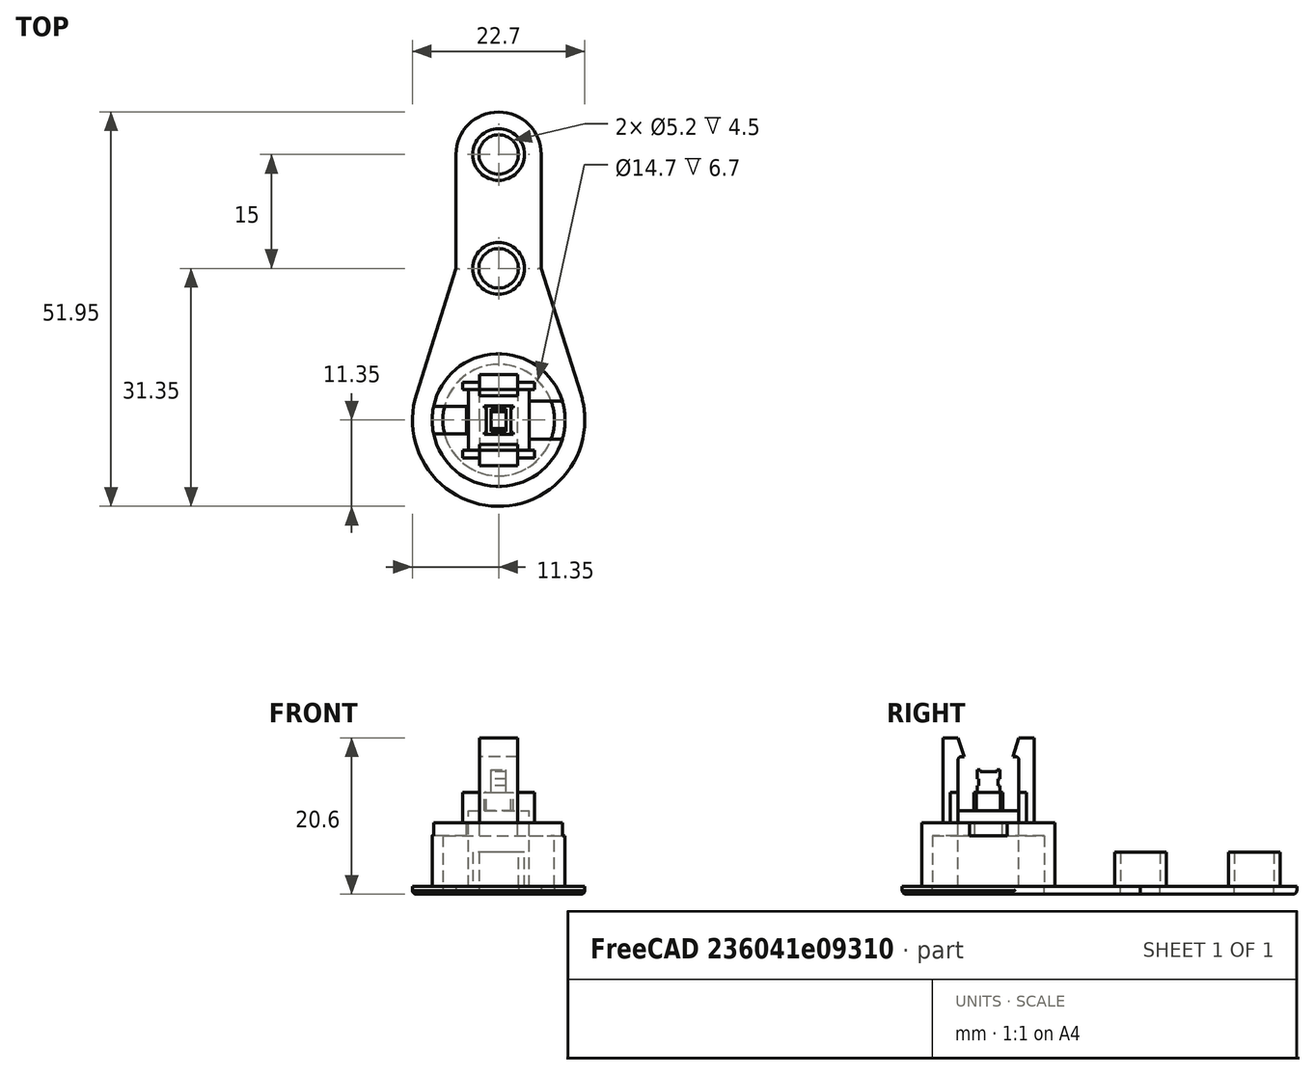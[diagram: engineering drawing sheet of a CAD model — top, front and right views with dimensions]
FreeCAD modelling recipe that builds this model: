
FCSTD DOCUMENT  (FreeCAD 0.18R13728 (Git))
Label: test113_powerbutton
License: All rights reserved
LicenseURL: http://en.wikipedia.org/wiki/All_rights_reserved
objects: Sketcher::SketchObject×12, PartDesign::Pad×10, PartDesign::Body×3, PartDesign::Fillet×2, Part::MultiFuse×2, PartDesign::Pocket×1, PartDesign::Plane×1, Mesh::Feature×1, Part::Extrusion×1, Part::Fillet×1, PartDesign::FeatureBase×1
note: 45 computed .brp shape members not serialized (recipe doc carries the construction recipe); baked Part::Feature solids carry a one-line shape summary decoded from their .brp

FEATURE [Sketcher::SketchObject] Sketch
  MapMode = 5
  Support = -> [XY_Plane]
  sketch-geometry (4):
    g0: LineSegment StartX=-4 StartY=-4 StartZ=0 EndX=4 EndY=-4 EndZ=0
    g1: LineSegment StartX=4 StartY=-4 StartZ=0 EndX=4 EndY=4 EndZ=0
    g2: LineSegment StartX=4 StartY=4 StartZ=0 EndX=-4 EndY=4 EndZ=0
    g3: LineSegment StartX=-4 StartY=4 StartZ=0 EndX=-4 EndY=-4 EndZ=0
  constraints (11):
    c: Coincident(g0,g1)
    c: Coincident(g1,g2)
    c: Coincident(g2,g3)
    c: Coincident(g3,g0)
    c: Horizontal(g0)
    c: Horizontal(g2)
    c: Vertical(g1)
    c: Vertical(g3)
    c: Equal(g2,g3)
    c: Symmetric(g2,g0,g-1)
    c: Distance(g2) = 8
FEATURE [PartDesign::Pad] Pad
  Length = 10
  Length2 = 100
  Profile = -> Sketch
  Type = 0
FEATURE [Sketcher::SketchObject] Sketch001
  MapMode = 5
  Placement = pos=(0,0,10) rot=(0,0,1;0rad)
  Support = -> [Pad]
  sketch-geometry (12):
    g0: LineSegment StartX=-1.9 StartY=1.9 StartZ=0 EndX=1.9 EndY=1.9 EndZ=0
    g1: LineSegment StartX=1.9 StartY=-1.9 StartZ=0 EndX=-1.9 EndY=-1.9 EndZ=0
    g2: LineSegment StartX=1.9 StartY=1.6 StartZ=0 EndX=1.6 EndY=1.6 EndZ=0
    g3: LineSegment StartX=1.6 StartY=1.6 StartZ=0 EndX=1.6 EndY=-1.6 EndZ=0
    g4: LineSegment StartX=1.6 StartY=-1.6 StartZ=0 EndX=1.9 EndY=-1.6 EndZ=0
    g5: LineSegment StartX=-1.9 StartY=-1.6 StartZ=0 EndX=-1.6 EndY=-1.6 EndZ=0
    g6: LineSegment StartX=-1.6 StartY=-1.6 StartZ=0 EndX=-1.6 EndY=1.6 EndZ=0
    g7: LineSegment StartX=-1.6 StartY=1.6 StartZ=0 EndX=-1.9 EndY=1.6 EndZ=0
    g8: LineSegment StartX=-1.9 StartY=1.6 StartZ=0 EndX=-1.9 EndY=1.9 EndZ=0
    g9: LineSegment StartX=1.9 StartY=1.6 StartZ=0 EndX=1.9 EndY=1.9 EndZ=0
    g10: LineSegment StartX=1.9 StartY=-1.6 StartZ=0 EndX=1.9 EndY=-1.9 EndZ=0
    g11: LineSegment StartX=-1.9 StartY=-1.9 StartZ=0 EndX=-1.9 EndY=-1.6 EndZ=0
  constraints (36):
    c: Horizontal(g0)
    c: Horizontal(g1)
    c: Distance(g0) = 3.8
    c: Coincident(g2,g3)
    c: Coincident(g3,g4)
    c: Horizontal(g2)
    c: Horizontal(g4)
    c: Vertical(g3)
    c: Coincident(g5,g6)
    c: Coincident(g6,g7)
    c: Horizontal(g5)
    c: Horizontal(g7)
    c: Vertical(g6)
    c: Coincident(g8,g7)
    c: Coincident(g8,g0)
    c: Vertical(g8)
    c: Coincident(g9,g2)
    c: Coincident(g9,g0)
    c: Vertical(g9)
    c: Coincident(g10,g4)
    c: Coincident(g10,g1)
    c: Coincident(g11,g1)
    c: Coincident(g11,g5)
    c: Vertical(g11)
    c: Vertical(g10)
    c: Symmetric(g0,g1,g-1)
    c: Equal(g5,g7)
    c: Equal(g5,g2)
    c: Equal(g5,g4)
    c: Equal(g6,g3)
    c: Equal(g11,g10)
    c: Equal(g11,g8)
    c: Equal(g11,g9)
    c: Distance(g8) = 0.3
    c: Distance(g7) = 0.3
    c: Distance(g1,g0) = 3.8
FEATURE [PartDesign::Pad] Pad001
  BaseFeature = -> Pad
  Length = 2.4
  Length2 = 100
  Profile = -> Sketch001
  Type = 0
FEATURE [Sketcher::SketchObject] Sketch002
  MapMode = 5
  Placement = pos=(0,0,12.4) rot=(0,0,1;0rad)
  Support = -> [Pad001]
  sketch-geometry (4):
    g0: LineSegment StartX=-1 StartY=-1.5 StartZ=0 EndX=1 EndY=-1.5 EndZ=0
    g1: LineSegment StartX=1 StartY=-1.5 StartZ=0 EndX=1 EndY=1.5 EndZ=0
    g2: LineSegment StartX=1 StartY=1.5 StartZ=0 EndX=-1 EndY=1.5 EndZ=0
    g3: LineSegment StartX=-1 StartY=1.5 StartZ=0 EndX=-1 EndY=-1.5 EndZ=0
  constraints (11):
    c: Coincident(g0,g1)
    c: Coincident(g1,g2)
    c: Coincident(g2,g3)
    c: Coincident(g3,g0)
    c: Horizontal(g0)
    c: Horizontal(g2)
    c: Vertical(g1)
    c: Vertical(g3)
    c: Symmetric(g0,g1,g-1)
    c: Distance(g2) = 2
    c: Distance(g1) = 3
FEATURE [PartDesign::Pad] Pad002
  BaseFeature = -> Pad001
  Length = 3
  Length2 = 100
  Profile = -> Sketch002
  Type = 0
FEATURE [Sketcher::SketchObject] Sketch003
  ExternalGeometry = -> [Pad002]
  MapMode = 5
  Placement = pos=(1,0,0) rot=(0.57735,0.57735,0.57735;2.0944rad)
  Support = -> [Pad002]
  sketch-geometry (12):
    g0: LineSegment StartX=-1.5 StartY=13.3 StartZ=0 EndX=-1.25 EndY=13.3 EndZ=0
    g1: LineSegment StartX=-1.25 StartY=13.3 StartZ=0 EndX=-1.25 EndY=14.2 EndZ=0
    g2: LineSegment StartX=-1.25 StartY=14.2 StartZ=0 EndX=-1.5 EndY=14.2 EndZ=0
    g3: LineSegment StartX=-1.5 StartY=14.2 StartZ=0 EndX=-1.5 EndY=13.3 EndZ=0
    g4: LineSegment StartX=1.5 StartY=13.3 StartZ=0 EndX=1.25 EndY=13.3 EndZ=0
    g5: LineSegment StartX=1.25 StartY=13.3 StartZ=0 EndX=1.25 EndY=14.2 EndZ=0
    g6: LineSegment StartX=1.25 StartY=14.2 StartZ=0 EndX=1.5 EndY=14.2 EndZ=0
    g7: LineSegment StartX=1.5 StartY=14.2 StartZ=0 EndX=1.5 EndY=13.3 EndZ=0
    g8: LineSegment StartX=-1.1 StartY=15.4 StartZ=0 EndX=1.1 EndY=15.4 EndZ=0
    g9: LineSegment StartX=1.1 StartY=15.4 StartZ=0 EndX=1.1 EndY=15.1 EndZ=0
    g10: LineSegment StartX=1.1 StartY=15.1 StartZ=0 EndX=-1.1 EndY=15.1 EndZ=0
    g11: LineSegment StartX=-1.1 StartY=15.1 StartZ=0 EndX=-1.1 EndY=15.4 EndZ=0
  constraints (36):
    c: Coincident(g0,g1)
    c: Coincident(g1,g2)
    c: Coincident(g2,g3)
    c: Coincident(g3,g0)
    c: Horizontal(g0)
    c: Horizontal(g2)
    c: Vertical(g1)
    c: Vertical(g3)
    c: PointOnObject(g0,g-3)
    c: Coincident(g4,g5)
    c: Coincident(g5,g6)
    c: Coincident(g6,g7)
    c: Coincident(g7,g4)
    c: Horizontal(g4)
    c: Horizontal(g6)
    c: Vertical(g5)
    c: Vertical(g7)
    c: PointOnObject(g4,g-5)
    c: Coincident(g8,g9)
    c: Coincident(g9,g10)
    c: Coincident(g10,g11)
    c: Coincident(g11,g8)
    c: Horizontal(g8)
    c: Horizontal(g10)
    c: Vertical(g9)
    c: Vertical(g11)
    c: PointOnObject(g8,g-6)
    c: Distance(g0,g4) = 2.5
    c: Equal(g2,g6)
    c: Equal(g5,g1)
    c: DistanceY(g0,g4) = 0
    c: DistanceY(g-4,g0) = 0.9
    c: Distance(g10) = 2.2
    c: Distance(g11) = 0.3
    c: Symmetric(g10,g9,g-2)
    c: Distance(g1) = 0.9
FEATURE [PartDesign::Pocket] Pocket
  BaseFeature = -> Pad002
  Length = 5
  Length2 = 100
  Profile = -> Sketch003
  Type = 1
FEATURE [PartDesign::Body] Body  label="Switch"
  Group = -> [Sketch,Pad,Sketch001,Pad001,Sketch002,Pad002,Sketch003,Pocket]
  Origin = -> Origin
  Tip = -> Pocket
FEATURE [Sketcher::SketchObject] Sketch004
  MapMode = 5
  Support = -> [XY_Plane002]
  sketch-geometry (2):
    g0: Circle CenterX=0 CenterY=0 CenterZ=0 NormalX=0 NormalY=0 NormalZ=1 AngleXU=0 Radius=7.35
    g1: Circle CenterX=0 CenterY=0 CenterZ=0 NormalX=0 NormalY=0 NormalZ=1 AngleXU=0 Radius=8.75
  constraints (4):
    c: Coincident(g0,g-1)
    c: Radius(g0) = 7.35
    c: Coincident(g1,g-1)
    c: Radius(g1) = 8.75
FEATURE [PartDesign::Pad] Pad003
  Length = 6.7
  Length2 = 100
  Profile = -> Sketch004
  Type = 0
FEATURE [Sketcher::SketchObject] Sketch005
  ExternalGeometry = -> [Pad003]
  MapMode = 5
  Placement = pos=(0,0,6.7) rot=(0,0,1;0rad)
  Support = -> [Pad003]
  sketch-geometry (20):
    g0: ArcOfCircle CenterX=0 CenterY=0 CenterZ=0 NormalX=0 NormalY=0 NormalZ=1 AngleXU=0 Radius=8.75 StartAngle=0.289752 EndAngle=2.9344
    g1: LineSegment StartX=-4.2276 StartY=0 StartZ=0 EndX=-4.2276 EndY=1.8 EndZ=0
    g2: LineSegment StartX=-4.2276 StartY=1.8 StartZ=0 EndX=-8.56286 EndY=1.8 EndZ=0
    g3: LineSegment StartX=4.05 StartY=0 StartZ=0 EndX=4.05 EndY=2.5 EndZ=0
    g4: LineSegment StartX=4.05 StartY=2.5 StartZ=0 EndX=8.38525 EndY=2.5 EndZ=0
    g5: GeomPoint X=8.75 Y=0 Z=0
    g6: GeomPoint X=-8.75 Y=0 Z=0
    g7: LineSegment StartX=-2.5 StartY=0 StartZ=0 EndX=-2.5 EndY=4 EndZ=0
    g8: LineSegment StartX=-2.5 StartY=4 StartZ=0 EndX=2.5 EndY=4 EndZ=0
    g9: LineSegment StartX=2.5 StartY=4 StartZ=0 EndX=2.5 EndY=0 EndZ=0
    g10: ArcOfCircle CenterX=0 CenterY=0 CenterZ=0 NormalX=0 NormalY=0 NormalZ=1 AngleXU=0 Radius=8.75 StartAngle=3.34879 EndAngle=5.99343
    g11: LineSegment StartX=-4.2276 StartY=0 StartZ=0 EndX=-4.2276 EndY=-1.8 EndZ=0
    g12: LineSegment StartX=-4.2276 StartY=-1.8 StartZ=0 EndX=-8.56286 EndY=-1.8 EndZ=0
    g13: LineSegment StartX=4.05 StartY=0 StartZ=0 EndX=4.05 EndY=-2.5 EndZ=0
    g14: LineSegment StartX=4.05 StartY=-2.5 StartZ=0 EndX=8.38525 EndY=-2.5 EndZ=0
    g15: GeomPoint X=8.75 Y=0 Z=0
    g16: GeomPoint X=-8.75 Y=0 Z=0
    g17: LineSegment StartX=-2.5 StartY=0 StartZ=0 EndX=-2.5 EndY=-4 EndZ=0
    g18: LineSegment StartX=-2.5 StartY=-4 StartZ=0 EndX=2.5 EndY=-4 EndZ=0
    g19: LineSegment StartX=2.5 StartY=-4 StartZ=0 EndX=2.5 EndY=0 EndZ=0
  constraints (55):
    c: Coincident(g0,g-1)
    c: PointOnObject(g0,g-3)
    c: PointOnObject(g1,g-1)
    c: Vertical(g1)
    c: Coincident(g1,g2)
    c: Coincident(g2,g0)
    c: Horizontal(g2)
    c: PointOnObject(g3,g-1)
    c: Vertical(g3)
    c: Coincident(g3,g4)
    c: Coincident(g4,g0)
    c: Horizontal(g4)
    c: PointOnObject(g5,g-3)
    c: PointOnObject(g6,g-3)
    c: PointOnObject(g6,g-1)
    c: PointOnObject(g5,g-1)
    c: DistanceX(g3,g5) = 4.7
    c: Distance(g3) = 2.5
    c: Distance(g1) = 1.8
    c: PointOnObject(g7,g-1)
    c: Vertical(g7)
    c: Coincident(g7,g8)
    c: Horizontal(g8)
    c: Coincident(g8,g9)
    c: PointOnObject(g9,g-1)
    c: Vertical(g9)
    c: Distance(g8) = 5
    c: Symmetric(g7,g9,g-1)
    c: Distance(g7) = 4
    c: Vertical(g11)
    c: Coincident(g11,g12)
    c: Coincident(g12,g10)
    c: Horizontal(g12)
    c: Vertical(g13)
    c: Coincident(g13,g14)
    c: Coincident(g14,g10)
    c: Horizontal(g14)
    c: Vertical(g17)
    c: Coincident(g17,g18)
    c: Horizontal(g18)
    c: Coincident(g18,g19)
    c: Vertical(g19)
    c: Symmetric(g17,g19,g-1)
    c: PointOnObject(g10,g-3)
    c: Coincident(g11,g1)
    c: PointOnObject(g10,g-3)
    c: Coincident(g13,g3)
    c: Coincident(g17,g7)
    c: PointOnObject(g10,g-1)
    c: Equal(g2,g4)
    c: Equal(g1,g11)
    c: Equal(g4,g2)
    c: Equal(g3,g13)
    c: Equal(g7,g17)
    c: Equal(g8,g18)
FEATURE [PartDesign::Pad] Pad004
  BaseFeature = -> Pad003
  Length = 1.7
  Length2 = 100
  Profile = -> Sketch005
  Type = 0
FEATURE [Sketcher::SketchObject] Sketch006
  ExternalGeometry = -> [Pad004]
  MapMode = 5
  Placement = pos=(0,0,8.4) rot=(0,0,1;0rad)
  Support = -> [Pad004]
  sketch-geometry (10):
    g0: LineSegment StartX=-4.75 StartY=5 StartZ=0 EndX=4.75 EndY=5 EndZ=0
    g1: LineSegment StartX=4.75 StartY=5 StartZ=0 EndX=4.75 EndY=4 EndZ=0
    g2: LineSegment StartX=4.75 StartY=4 StartZ=0 EndX=-4.75 EndY=4 EndZ=0
    g3: LineSegment StartX=-4.75 StartY=4 StartZ=0 EndX=-4.75 EndY=5 EndZ=0
    g4: GeomPoint X=0 Y=4 Z=0
    g5: LineSegment StartX=4.75 StartY=-5 StartZ=0 EndX=-4.75 EndY=-5 EndZ=0
    g6: LineSegment StartX=-4.75 StartY=-5 StartZ=0 EndX=-4.75 EndY=-4 EndZ=0
    g7: LineSegment StartX=-4.75 StartY=-4 StartZ=0 EndX=4.75 EndY=-4 EndZ=0
    g8: LineSegment StartX=4.75 StartY=-4 StartZ=0 EndX=4.75 EndY=-5 EndZ=0
    g9: GeomPoint X=1.4e-11 Y=-4 Z=0
  constraints (25):
    c: Coincident(g0,g1)
    c: Coincident(g1,g2)
    c: Coincident(g2,g3)
    c: Coincident(g3,g0)
    c: Horizontal(g0)
    c: Horizontal(g2)
    c: Vertical(g1)
    c: Vertical(g3)
    c: PointOnObject(g4,g-2)
    c: PointOnObject(g4,g-3)
    c: Symmetric(g2,g1,g4)
    c: Distance(g1) = 1
    c: Distance(g0) = 9.5
    c: Coincident(g5,g6)
    c: Coincident(g6,g7)
    c: Coincident(g7,g8)
    c: Coincident(g8,g5)
    c: Horizontal(g5)
    c: Horizontal(g7)
    c: Vertical(g6)
    c: Vertical(g8)
    c: Symmetric(g7,g6,g9)
    c: Distance(g6) = 1
    c: Distance(g5) = 9.5
    c: Symmetric(g6,g1,g-1)
FEATURE [PartDesign::Pad] Pad005
  BaseFeature = -> Pad004
  Length = 4
  Length2 = 100
  Profile = -> Sketch006
  Type = 0
FEATURE [PartDesign::Plane] DatumPlane
  AttachmentOffset = pos=(0,0,0) rot=(0.57735,0.57735,-0.57735;2.0944rad)
  MapMode = 45
  Placement = pos=(0,4,7.55) rot=(0.57735,-0.57735,-0.57735;2.0944rad)
  Support = -> [Pad005]
FEATURE [Sketcher::SketchObject] Sketch007
  ExternalGeometry = -> [Pad005]
  MapMode = 5
  Placement = pos=(0,4,7.55) rot=(0.57735,-0.57735,-0.57735;2.0944rad)
  Support = -> [DatumPlane]
  sketch-geometry (18):
    g0: LineSegment [constr] StartX=8.956e-09 StartY=0.85 StartZ=0 EndX=8.956e-09 EndY=9.55 EndZ=0
    g1: LineSegment [constr] StartX=8.956e-09 StartY=9.55 StartZ=0 EndX=0.8 EndY=9.55 EndZ=0
    g2: LineSegment StartX=0.8 StartY=9.55 StartZ=0 EndX=0 EndY=12.05 EndZ=0
    g3: LineSegment StartX=0 StartY=12.05 StartZ=0 EndX=-2 EndY=12.05 EndZ=0
    g4: LineSegment StartX=-2 StartY=12.05 StartZ=0 EndX=-2 EndY=0.85 EndZ=0
    g5: LineSegment StartX=-2 StartY=0.85 StartZ=0 EndX=8.956e-09 EndY=0.85 EndZ=0
    g6: LineSegment StartX=8.956e-09 StartY=0.85 StartZ=0 EndX=8.956e-09 EndY=9.15 EndZ=0
    g7: LineSegment StartX=0.4 StartY=9.55 StartZ=0 EndX=0.8 EndY=9.55 EndZ=0
    g8: ArcOfCircle CenterX=0.4 CenterY=9.15 CenterZ=0 NormalX=0 NormalY=0 NormalZ=1 AngleXU=0 Radius=0.4 StartAngle=1.5708 EndAngle=3.14159
    g9: LineSegment [constr] StartX=8 StartY=0.85 StartZ=0 EndX=8 EndY=9.55 EndZ=0
    g10: LineSegment [constr] StartX=8 StartY=9.55 StartZ=0 EndX=7.2 EndY=9.55 EndZ=0
    g11: LineSegment StartX=7.2 StartY=9.55 StartZ=0 EndX=8 EndY=12.05 EndZ=0
    g12: LineSegment StartX=8 StartY=12.05 StartZ=0 EndX=10 EndY=12.05 EndZ=0
    g13: LineSegment StartX=10 StartY=12.05 StartZ=0 EndX=10 EndY=0.85 EndZ=0
    g14: LineSegment StartX=10 StartY=0.85 StartZ=0 EndX=8 EndY=0.85 EndZ=0
    g15: LineSegment StartX=8 StartY=0.85 StartZ=0 EndX=8 EndY=9.15 EndZ=0
    g16: LineSegment StartX=7.6 StartY=9.55 StartZ=0 EndX=7.2 EndY=9.55 EndZ=0
    g17: ArcOfCircle CenterX=7.6 CenterY=9.15 CenterZ=0 NormalX=0 NormalY=0 NormalZ=1 AngleXU=0 Radius=0.4 StartAngle=0 EndAngle=1.5708
  constraints (48):
    c: Coincident(g0,g-3)
    c: Vertical(g0)
    c: Coincident(g0,g1)
    c: Horizontal(g1)
    c: Coincident(g1,g2)
    c: PointOnObject(g2,g-2)
    c: Coincident(g2,g3)
    c: Horizontal(g3)
    c: Coincident(g3,g4)
    c: Vertical(g4)
    c: Coincident(g4,g5)
    c: Coincident(g5,g0)
    c: Horizontal(g5)
    c: Distance(g4) = 11.2
    c: Distance(g3) = 2
    c: Distance(g0,g2) = 2.5
    c: Coincident(g0,g6)
    c: Vertical(g6)
    c: Coincident(g7,g1)
    c: Tangent(g6,g8) = 1.5708
    c: Tangent(g7,g8) = 1.5708
    c: PointOnObject(g7,g1)
    c: Symmetric(g0,g1,g7)
    c: Vertical(g9)
    c: Coincident(g9,g10)
    c: Horizontal(g10)
    c: Coincident(g10,g11)
    c: Coincident(g11,g12)
    c: Horizontal(g12)
    c: Coincident(g12,g13)
    c: Vertical(g13)
    c: Coincident(g13,g14)
    c: Coincident(g14,g9)
    c: Horizontal(g14)
    c: Distance(g9,g11) = 2.5
    c: Coincident(g9,g15)
    c: Vertical(g15)
    c: Coincident(g16,g10)
    c: Tangent(g15,g17) = -1.5708
    c: Tangent(g16,g17) = -1.5708
    c: PointOnObject(g16,g10)
    c: Symmetric(g9,g10,g16)
    c: Symmetric(g0,g9,g-4)
    c: PointOnObject(g11,g9)
    c: Equal(g13,g4)
    c: Distance(g0,g1) = 0.8
    c: Equal(g1,g10)
    c: Equal(g3,g12)
FEATURE [PartDesign::Pad] Pad006
  BaseFeature = -> Pad005
  Length = 5
  Length2 = 100
  Midplane = true
  Profile = -> Sketch007
  Type = 0
FEATURE [Sketcher::SketchObject] Sketch008
  ExternalGeometry = -> [Pad006]
  MapMode = 5
  Placement = pos=(0,0,0) rot=(1,0,0;3.14159rad)
  Support = -> [Pad006]
  sketch-geometry (4):
    g0: GeomPoint X=-7.35 Y=0 Z=0
    g1: Circle CenterX=0 CenterY=0 CenterZ=0 NormalX=0 NormalY=0 NormalZ=1 AngleXU=0 Radius=11.35
    g2: GeomPoint X=-11.35 Y=0 Z=0
    g3: Circle CenterX=0 CenterY=0 CenterZ=0 NormalX=0 NormalY=0 NormalZ=1 AngleXU=0 Radius=7.35
  constraints (8):
    c: PointOnObject(g0,g-3)
    c: PointOnObject(g0,g-1)
    c: Coincident(g1,g-1)
    c: PointOnObject(g2,g1)
    c: PointOnObject(g2,g-1)
    c: Distance(g0,g2) = 4
    c: Coincident(g3,g-1)
    c: PointOnObject(g0,g3)
FEATURE [PartDesign::Pad] Pad007
  BaseFeature = -> Pad006
  Length = 1
  Length2 = 100
  Profile = -> Sketch008
  Type = 0
FEATURE [PartDesign::Fillet] Fillet
  Base = -> Pad007 [Edge78]
  BaseFeature = -> Pad007
  Radius = 0.5
FEATURE [PartDesign::Body] Body002
  Group = -> [Sketch004,Pad003,Sketch005,Pad004,Sketch006,Pad005,DatumPlane,Sketch007,Pad006,Sketch008,Pad007,Fillet]
  Origin = -> Origin002
  Tip = -> Fillet
FEATURE [Sketcher::SketchObject] Sketch009
  AttachmentOffset = pos=(0,20,0) rot=(0,0,1;0rad)
  MapMode = 5
  Placement = pos=(0,20,0) rot=(0,0,1;0rad)
  Support = -> [XY_Plane003]
  sketch-geometry (4):
    g0: Circle CenterX=0 CenterY=0 CenterZ=0 NormalX=0 NormalY=0 NormalZ=1 AngleXU=0 Radius=2.6
    g1: Circle CenterX=0 CenterY=0 CenterZ=0 NormalX=0 NormalY=0 NormalZ=1 AngleXU=0 Radius=5.6
    g2: GeomPoint X=-5.6 Y=0 Z=0
    g3: GeomPoint X=-2.6 Y=0 Z=0
  constraints (8):
    c: Coincident(g0,g-1)
    c: Radius(g0) = 2.6
    c: Coincident(g1,g-1)
    c: PointOnObject(g2,g1)
    c: PointOnObject(g3,g0)
    c: PointOnObject(g3,g-1)
    c: PointOnObject(g2,g-1)
    c: Distance(g2,g3) = 3
FEATURE [PartDesign::Pad] Pad008
  Length = 1
  Length2 = 100
  Profile = -> Sketch009
  Reversed = true
  Type = 0
FEATURE [Mesh::Feature] Mesh  label="Fusion001 (Meshed)"
FEATURE [PartDesign::Body] Body003
  Group = -> [Sketch009,Pad008,Sketch010,Pad009,Fillet001]
  Origin = -> Origin003
  Tip = -> Fillet001
FEATURE [Sketcher::SketchObject] Sketch010
  ExternalGeometry = -> [Pad008]
  MapMode = 5
  Support = -> [Fillet001]
  sketch-geometry (6):
    g0: GeomPoint X=2.12384 Y=21.4998 Z=0
    g1: Circle CenterX=0 CenterY=20 CenterZ=0 NormalX=0 NormalY=0 NormalZ=1 AngleXU=0 Radius=2.6
    g2: GeomPoint X=2.12384 Y=21.4998 Z=0
    g3: Circle CenterX=0 CenterY=20 CenterZ=0 NormalX=0 NormalY=0 NormalZ=1 AngleXU=0 Radius=3.4
    g4: GeomPoint X=0 Y=23.4 Z=0
    g5: GeomPoint X=0 Y=22.6 Z=0
  constraints (10):
    c: PointOnObject(g0,g-3)
    c: Coincident(g1,g-3)
    c: PointOnObject(g2,g1)
    c: Coincident(g2,g0)
    c: Coincident(g3,g1)
    c: PointOnObject(g4,g3)
    c: PointOnObject(g5,g1)
    c: PointOnObject(g5,g-2)
    c: PointOnObject(g4,g-2)
    c: Distance(g5,g4) = 0.8
FEATURE [PartDesign::Pad] Pad009
  BaseFeature = -> Pad008
  Length = 4.5
  Length2 = 100
  Profile = -> Sketch010
  Type = 0
FEATURE [PartDesign::Fillet] Fillet001
  Base = -> Pad009 [Edge3]
  BaseFeature = -> Pad009
  Radius = 0.5
FEATURE [Sketcher::SketchObject] Sketch011
  ExternalGeometry = -> [Fillet,Fillet001,Clone]
  Placement = pos=(0,0,0) rot=(0,1,0;3.14159rad)
  sketch-geometry (12):
    g0: ArcOfCircle CenterX=0 CenterY=0 CenterZ=0 NormalX=0 NormalY=0 NormalZ=1 AngleXU=0 Radius=11.3495 StartAngle=2.83659 EndAngle=6.58819
    g1: LineSegment StartX=-10.8257 StartY=3.40824 StartZ=0 EndX=-5.60231 EndY=19.9994 EndZ=0
    g2: LineSegment StartX=-5.60231 StartY=19.9994 StartZ=0 EndX=-5.60231 EndY=35 EndZ=0
    g3: LineSegment StartX=5.60231 StartY=35 StartZ=0 EndX=5.60231 EndY=19.9994 EndZ=0
    g4: LineSegment StartX=10.8257 StartY=3.40824 StartZ=0 EndX=5.60231 EndY=19.9994 EndZ=0
    g5: GeomPoint X=0 Y=3.40824 Z=0
    g6: Circle CenterX=0 CenterY=20 CenterZ=0 NormalX=0 NormalY=0 NormalZ=1 AngleXU=0 Radius=2.6
    g7: Circle CenterX=0 CenterY=0 CenterZ=0 NormalX=0 NormalY=0 NormalZ=1 AngleXU=0 Radius=7.35
    g8: GeomPoint X=-1.91318 Y=7.09664 Z=0
    g9: GeomPoint X=-1.91318 Y=7.09664 Z=0
    g10: ArcOfCircle CenterX=0 CenterY=35 CenterZ=0 NormalX=0 NormalY=0 NormalZ=1 AngleXU=0 Radius=5.60231 StartAngle=6.28318 EndAngle=9.42477
    g11: Circle CenterX=0 CenterY=35 CenterZ=0 NormalX=0 NormalY=0 NormalZ=1 AngleXU=0 Radius=2.6
  constraints (23):
    c: Coincident(g0,g-1)
    c: Tangent(g0,g1) = 1.5708
    c: Coincident(g4,g0)
    c: PointOnObject(g5,g-2)
    c: Symmetric(g0,g0,g5)
    c: Coincident(g4,g3)
    c: Coincident(g1,g2)
    c: Symmetric(g3,g1,g-2)
    c: Vertical(g2)
    c: Coincident(g7,g-1)
    c: PointOnObject(g8,g7)
    c: Coincident(g9,g8)
    c: Coincident(g6,g-6)
    c: Radius(g6) = 2.6
    c: Distance(g1) = 17.394
    c: Equal(g1,g4)
    c: Coincident(g10,g-7)
    c: Coincident(g10,g2)
    c: Coincident(g10,g3)
    c: Angle(g10) = 3.14159
    c: Tangent(g3,g10)
    c: Coincident(g11,g10)
    c: Equal(g11,g6)
FEATURE [Part::Extrusion] Extrude
  Base = -> Sketch011
  Dir = (0,0,-1)
  DirMode = 2
  FaceMakerClass = Part::FaceMakerBullseye
  LengthFwd = 1
  LengthRev = 0
  Solid = true
  Symmetric = false
FEATURE [Part::MultiFuse] Fusion
  Shapes = -> [Body003,Body002,Clone]
FEATURE [Part::Fillet] Fillet002
  Base = -> Extrude
  Edges = 2 edges r=0.49: [Edge16,Edge18]
FEATURE [Part::MultiFuse] Fusion001
  Shapes = -> [Fillet002,Fusion]
FEATURE [PartDesign::FeatureBase] Clone
  BaseFeature = -> Body003
  Placement = pos=(0,15,0) rot=(0,0,1;0rad)
